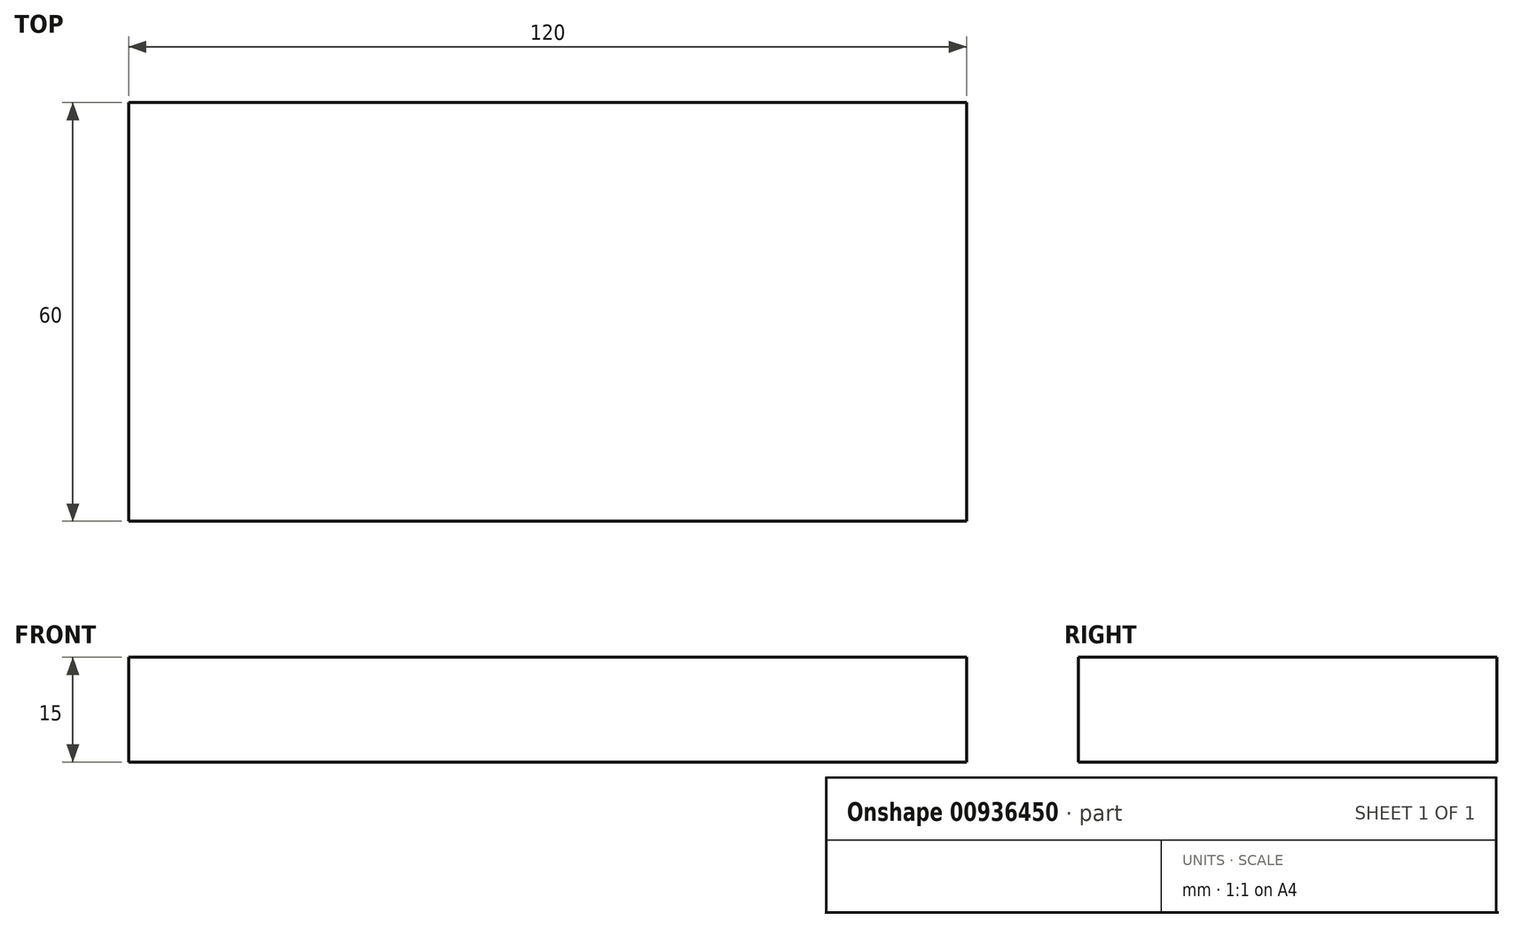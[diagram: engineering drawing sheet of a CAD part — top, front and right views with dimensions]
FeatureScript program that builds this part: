
annotation { "Feature Type Name" : "Feature", "Feature Type Description" : "" }
export const myFeature = defineFeature(function(context is Context, id is Id, definition is map)
    precondition{}
    {
        {
            assignVariable(context, id + "F0", {"name" : "sirka", "anyValue" : 120});
        }
        {
            assignVariable(context, id + "F1", {"name" : "d2", "anyValue" : getVariable(context, 'sirka') / 8});
        }
        {
            var Q0;
            Q0=qCreatedBy(makeId("Top.planeOp"),FACE);
            var sketch = newSketch(context, id + "F2", { "sketchPlane" : qUnion([Q0])});
            skLineSegment(sketch, "E0.bottom", {"start": v(-60, 30) * mm, "end": v(60, 30) * mm});
            skLineSegment(sketch, "E0.top", {"start": v(-60, -30) * mm, "end": v(60, -30) * mm});
            skLineSegment(sketch, "E0.left", {"start": v(-60, 30) * mm, "end": v(-60, -30) * mm});
            skLineSegment(sketch, "E0.right", {"start": v(60, 30) * mm, "end": v(60, -30) * mm});
            skSolve(sketch);
        }
        {
            var Q0;
            Q0 = qSketchRegion(id + "F2", true);
            extrude(context, id + "F3", {"entities" : qUnion([Q0]), "depth" : (getVariable(context, 'd2')) * mm, "offsetDistance" : 25 * mm});
        }
    });
